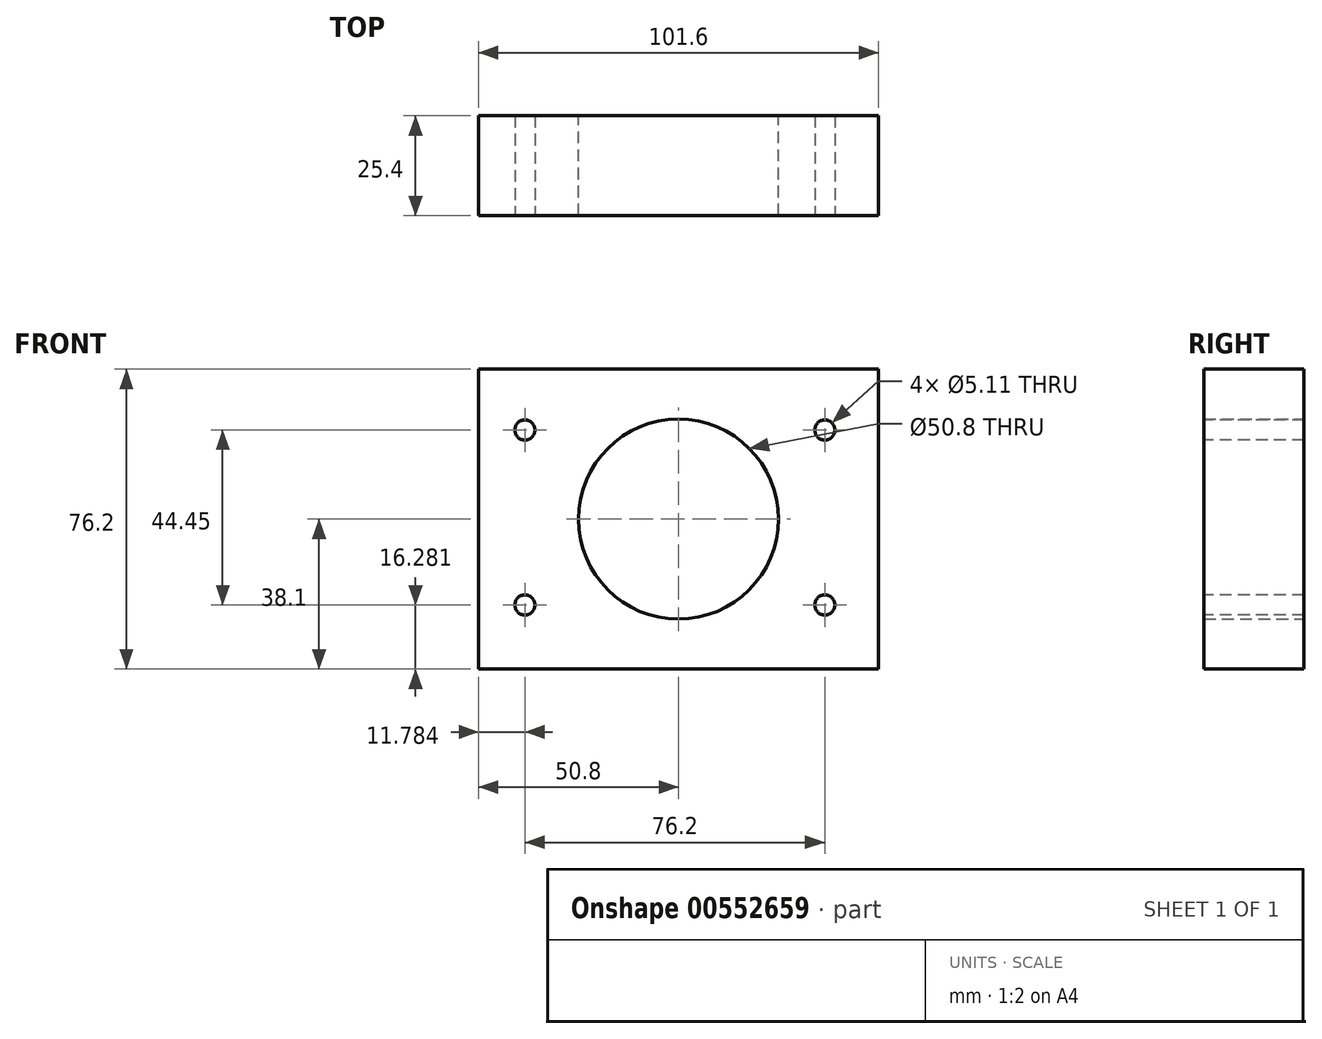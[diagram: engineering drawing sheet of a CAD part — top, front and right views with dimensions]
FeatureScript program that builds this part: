
annotation { "Feature Type Name" : "Feature", "Feature Type Description" : "" }
export const myFeature = defineFeature(function(context is Context, id is Id, definition is map)
    precondition{}
    {
        {
            var Q0;
            Q0=qCreatedBy(makeId("Front.planeOp"),FACE);
            var sketch = newSketch(context, id + "F0", { "sketchPlane" : qUnion([Q0])});
            skLineSegment(sketch, "E0.bottom", {"start": v(50.8, -38.1) * mm, "end": v(-50.8, -38.1) * mm});
            skLineSegment(sketch, "E0.top", {"start": v(50.8, 38.1) * mm, "end": v(-50.8, 38.1) * mm});
            skLineSegment(sketch, "E0.left", {"start": v(50.8, -38.1) * mm, "end": v(50.8, 38.1) * mm});
            skLineSegment(sketch, "E0.right", {"start": v(-50.8, -38.1) * mm, "end": v(-50.8, 38.1) * mm});
            skPoint(sketch, "E0.middle", {"position": v(0, 0) * mm});
            skCircle(sketch, "E1", {"center": v(0, 0) * mm, "radius": 25.4 * mm});
            skSolve(sketch);
        }
        {
            var Q0;
            Q0 = qSketchRegion(id + "F0", true);
            extrude(context, id + "F1", {"entities" : qUnion([Q0]), "depth" : 25.4 * mm, "offsetDistance" : 25.4 * mm});
        }
        {
            var Q0;
            Q0=makeQuery(id+"F1.opExtrude","CAP_FACE",FACE,{"disambiguationData":[OSD([sQuery(id+"F0.wireOp",EDGE,"E0.bottom"),sQuery(id+"F0.wireOp",EDGE,"E0.top"),sQuery(id+"F0.wireOp",EDGE,"E0.left"),sQuery(id+"F0.wireOp",EDGE,"E0.right"),sQuery(id+"F0.wireOp",EDGE,"E1")])],"isStart":false});
            var sketch = newSketch(context, id + "F2", { "sketchPlane" : qUnion([Q0])});
            skPoint(sketch, "E2", {"position": v(-39.02, 22.63) * mm});
            skPoint(sketch, "E3", {"position": v(-39.02, -21.82) * mm});
            skPoint(sketch, "E4", {"position": v(37.18, -21.82) * mm});
            skPoint(sketch, "E5", {"position": v(37.18, 22.63) * mm});
            skSolve(sketch);
        }
        {
            var Q0;
            Q0=sQuery(id+"F2.wireOp",VERTEX,"E2");
            var Q1;
            Q1=sQuery(id+"F2.wireOp",VERTEX,"E3");
            var Q2;
            Q2=sQuery(id+"F2.wireOp",VERTEX,"E4");
            var Q3;
            Q3=sQuery(id+"F2.wireOp",VERTEX,"E5");
            var Q4;
            Q4=makeQuery(id+"F1.opExtrude","SWEPT_BODY",BODY,{"disambiguationData":[OSD([sQuery(id+"F0.wireOp",EDGE,"E0.bottom"),sQuery(id+"F0.wireOp",EDGE,"E0.top"),sQuery(id+"F0.wireOp",EDGE,"E0.left"),sQuery(id+"F0.wireOp",EDGE,"E0.right"),sQuery(id+"F0.wireOp",EDGE,"E1")])]});
            hole(context, id + "F3", {"style" : HoleStyle.SIMPLE, "endStyle" : HoleEndStyle.THROUGH, "standardTappedOrClearance" : lookupTablePath({ "standard" : "ANSI", "engagement" : "75%", "pitch" : "20 tpi", "size" : "1/4", "type" : "Tapped" }), "standardBlindInLast" : lookupTablePath({ "standard" : "ANSI", "engagement" : "75%", "pitch" : "20 tpi", "size" : "1/4", "type" : "Tapped" }), "holeDiameter" : 5.1 * mm, "showTappedDepth" : true, "isTappedThrough" : true, "tappedDepth" : 12.7 * mm, "tapClearance" : 3, "locations" : qUnion([Q0, Q1, Q2, Q3]), "scope" : qUnion([Q4]), "majorDiameter" : 6.35 * mm});
        }
    });
